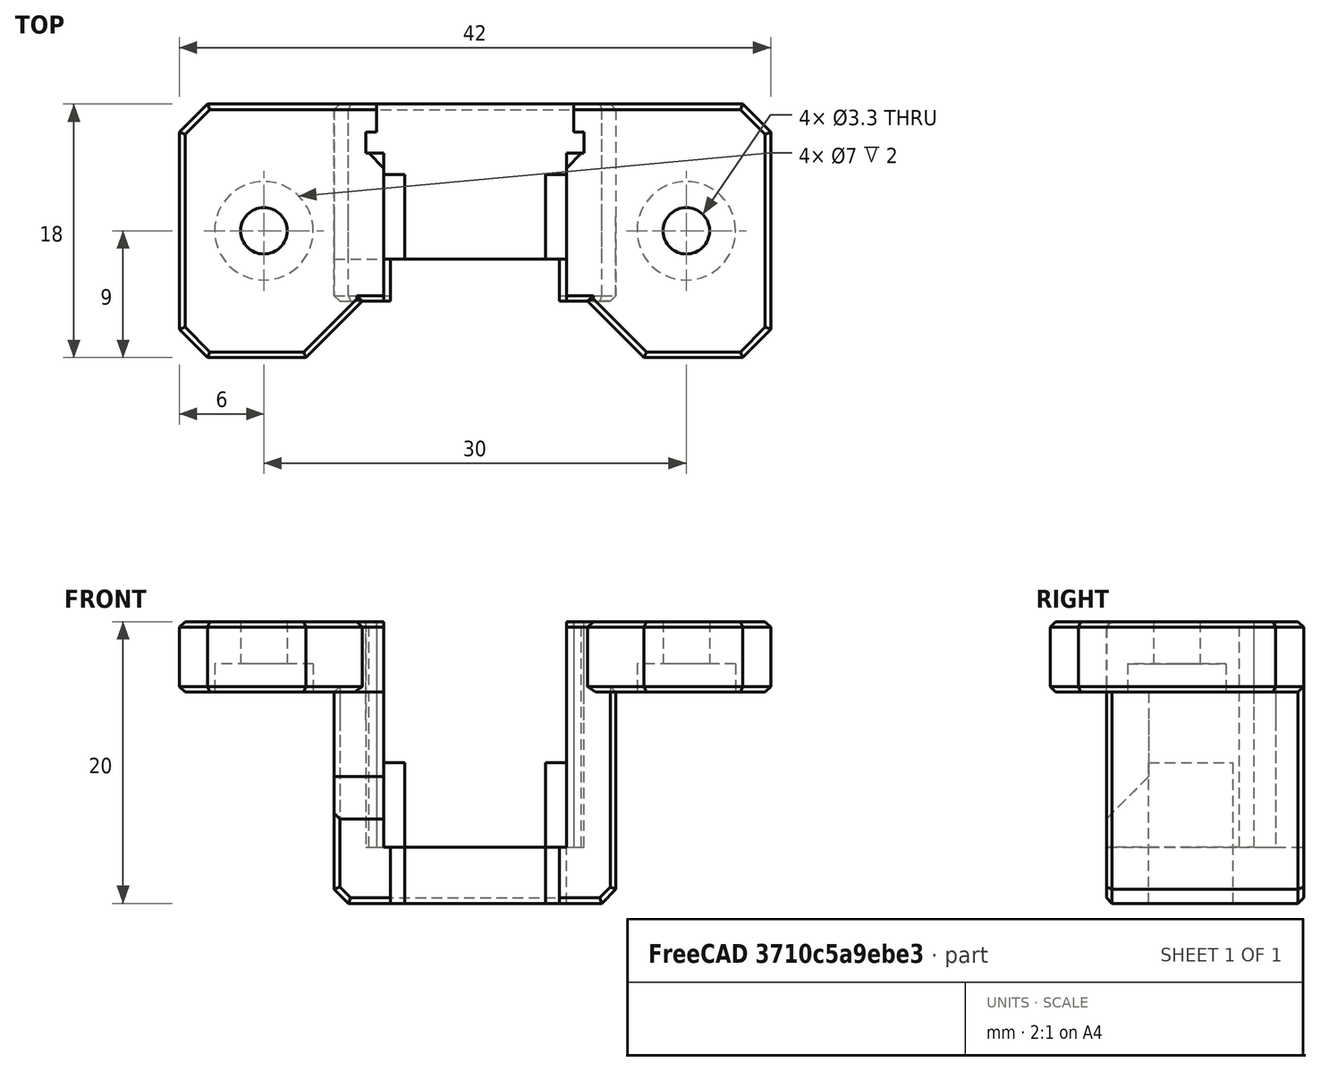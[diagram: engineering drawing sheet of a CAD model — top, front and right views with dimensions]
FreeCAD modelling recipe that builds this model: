
FCSTD DOCUMENT  (FreeCAD 0.18R16146 (Git))
Label: HTU2X-mounter
License: Other
LicenseURL: GPL3
objects: Part::Box×12, Part::MultiFuse×9, Part::Chamfer×7, Part::Cut×6, Part::Feature×6, Part::Cylinder×3, Part::MultiCommon×2
note: 45 computed .brp shape members not serialized (recipe doc carries the construction recipe); baked Part::Feature solids carry a one-line shape summary decoded from their .brp

FEATURE [Part::Box] Box  label="Cube"
  AttacherType = Attacher::AttachEngine3D
  Height = 9
  Length = 13
  Placement = pos=(-6.5,0,-2) rot=(0,0,1;0rad)
  Width = 15
FEATURE [Part::Box] Box001  label="Cube001"
  AttacherType = Attacher::AttachEngine3D
  Height = 2
  Length = 15.5
  Placement = pos=(-7.75,0,7) rot=(0,0,1;0rad)
  Width = 15
FEATURE [Part::MultiFuse] Fusion
  Shapes = -> [Box001,Box]
FEATURE [Part::Box] Box002  label="Cube002"
  AttacherType = Attacher::AttachEngine3D
  Height = 11
  Length = 20
  Placement = pos=(-10,0,0) rot=(0,0,1;0rad)
  Width = 19
FEATURE [Part::Cut] Cut
  Base = -> Box002
  Tool = -> Fusion
FEATURE [Part::Box] Box003  label="Cube003"
  AttacherType = Attacher::AttachEngine3D
  Height = 10
  Length = 14
  Placement = pos=(-7,0,8) rot=(0,0,1;0rad)
  Width = 15
FEATURE [Part::Cut] Cut001
  Base = -> Cut
  Placement = pos=(0,4e-15,19) rot=(-1,0,0;1.5708rad)
  Tool = -> Box003
FEATURE [Part::Cylinder] Cylinder
  Angle = 360
  AttacherType = Attacher::AttachEngine3D
  Height = 10
  Placement = pos=(0,4,15) rot=(0,0,1;0rad)
  Radius = 14
FEATURE [Part::Feature] Cylinder001
  Placement = pos=(0,4,12) rot=(0,0,1;0rad)
  shape: bbox 28 x 28 x 10 mm, 3 faces (baked)
FEATURE [Part::Feature] Cut001001  label="Cut002"
  Placement = pos=(0,4e-15,19) rot=(-1,0,0;1.5708rad)
  shape: bbox 20 x 11 x 19 mm, 21 faces (baked)
FEATURE [Part::MultiCommon] Common
  Placement = pos=(0,0,1) rot=(0,0,1;0rad)
  Shapes = -> [Cylinder001,Cut001001]
FEATURE [Part::Cut] Cut001002
  Base = -> Cut001
  Tool = -> Cylinder
FEATURE [Part::MultiFuse] Fusion001
  Shapes = -> [Cut001002,Common]
FEATURE [Part::Feature] Box004001  label="Cube005"
  Placement = pos=(-11,-4,0) rot=(0,0,1;0rad)
  shape: bbox 22 x 10 x 25 mm, 6 faces (baked)
FEATURE [Part::Feature] Fusion001001  label="Fusion002"
  shape: bbox 20 x 11 x 20 mm, 53 faces (baked)
FEATURE [Part::MultiCommon] Common001
  Placement = pos=(0,-3,0) rot=(0,0,1;0rad)
  Shapes = -> [Fusion001001,Box004001]
FEATURE [Part::MultiFuse] Fusion001002
  Shapes = -> [Fusion001,Common001]
FEATURE [Part::Box] Box004002  label="Cube006"
  AttacherType = Attacher::AttachEngine3D
  Height = 10
  Length = 12
  Placement = pos=(-6,-10,0) rot=(0,0,1;0rad)
  Width = 10
FEATURE [Part::Cut] Cut001003
  Base = -> Fusion001002
  Tool = -> Box004002
FEATURE [Part::Cylinder] Cylinder002
  Angle = 360
  AttacherType = Attacher::AttachEngine3D
  Height = 10
  Placement = pos=(0,0,0) rot=(-1,0,0;1.5708rad)
  Radius = 1.65
FEATURE [Part::Cylinder] Cylinder003
  Angle = 360
  AttacherType = Attacher::AttachEngine3D
  Height = 2
  Placement = pos=(0,8,1.8e-15) rot=(-1,0,0;1.5708rad)
  Radius = 3.5
FEATURE [Part::MultiFuse] Fusion001003
  Placement = pos=(-15,0,10) rot=(0,0,1;0rad)
  Shapes = -> [Cylinder003,Cylinder002]
FEATURE [Part::Feature] Fusion001003001  label="Fusion001004"
  Placement = pos=(15,0,10) rot=(0,0,1;0rad)
  shape: bbox 7 x 10 x 7 mm, 6 faces (baked)
FEATURE [Part::Box] Box004003  label="Cube007"
  AttacherType = Attacher::AttachEngine3D
  Height = 5
  Length = 13
  Placement = pos=(8,-7,15) rot=(0,0,1;0rad)
  Width = 18
FEATURE [Part::Box] Box004004  label="Cube008"
  AttacherType = Attacher::AttachEngine3D
  Height = 5
  Length = 13
  Placement = pos=(-21,-7,15) rot=(0,0,1;0rad)
  Width = 18
FEATURE [Part::MultiFuse] Fusion001003002
  Placement = pos=(0,-8,25) rot=(-1,0,0;1.5708rad)
  Shapes = -> [Fusion001003001,Fusion001003]
FEATURE [Part::Chamfer] Chamfer002
  Base = -> Cut001003
  Edges = 4 edges r=1: [Edge9,Edge16,Edge28,Edge125]
FEATURE [Part::Chamfer] Chamfer003
  Base = -> Chamfer002
  Edges = 27 edges r=0.4: [Edge1,Edge5,Edge7,Edge9,Edge11,Edge16,Edge39,Edge44,Edge47,Edge52,Edge53,Edge76,Edge77,Edge79,Edge80,Edge82,Edge89,Edge105,Edge116,Edge122,Edge139,Edge173,Edge191,Edge192,Edge212,Edge216,Edge220]
FEATURE [Part::Box] Box004005  label="Cube009"
  AttacherType = Attacher::AttachEngine3D
  Height = 10
  Length = 1.5
  Placement = pos=(-6.5,1,0) rot=(0,0,1;0rad)
  Width = 6
FEATURE [Part::Box] Box004006  label="Cube010"
  AttacherType = Attacher::AttachEngine3D
  Height = 10
  Length = 1.5
  Placement = pos=(5,1,0) rot=(0,0,1;0rad)
  Width = 6
FEATURE [Part::MultiFuse] Fusion001003005
  Shapes = -> [Box004006,Box004005]
FEATURE [Part::MultiFuse] Fusion001003006
  Shapes = -> [Box004004,Box004003]
FEATURE [Part::Chamfer] Chamfer
  Base = -> Fusion001003006
  Edges = 4 edges r=2: [Edge1,Edge3,Edge17,Edge19]
FEATURE [Part::Chamfer] Chamfer004
  Base = -> Chamfer
  Edges = 2 edges r=4: [Edge17,Edge36]
FEATURE [Part::Chamfer] Chamfer005
  Base = -> Chamfer004
  Edges = 28 edges r=0.4: [Edge1,Edge2,Edge3,Edge4,Edge5,Edge6,Edge7,Edge8,Edge11,Edge13,Edge16,Edge18,Edge19,Edge21,Edge22,Edge23,Edge24,Edge25,Edge26,Edge27,Edge28,Edge31,Edge32,Edge34,Edge36,Edge38,Edge40,Edge42]
FEATURE [Part::Cut] Cut001004
  Base = -> Chamfer005
  Tool = -> Fusion001003002
FEATURE [Part::MultiFuse] Fusion001003007
  Shapes = -> [Cut001004,Chamfer003]
FEATURE [Part::Box] Box004007  label="Cube011"
  AttacherType = Attacher::AttachEngine3D
  Height = 9
  Length = 10
  Placement = pos=(-10,-10,6) rot=(0,0,1;0rad)
  Width = 10
FEATURE [Part::Chamfer] Chamfer006
  Base = -> Box004007
  Edges = 1 edges r=3: [Edge11]
FEATURE [Part::Cut] Cut001005
  Base = -> Fusion001003007
  Placement = pos=(0,1,0) rot=(0,0,1;0rad)
  Tool = -> Chamfer006
FEATURE [Part::Box] Box004008  label="Cube012"
  AttacherType = Attacher::AttachEngine3D
  Height = 20
  Length = 2
  Placement = pos=(6.5,6.5,0) rot=(0,0,1;0rad)
  Width = 2
FEATURE [Part::Box] Box004009  label="Cube013"
  AttacherType = Attacher::AttachEngine3D
  Height = 20
  Length = 2
  Placement = pos=(-8.5,6.5,0) rot=(0,0,1;0rad)
  Width = 2
FEATURE [Part::MultiFuse] Fusion001003008
  Shapes = -> [Cut001005,Box004008,Box004009]
FEATURE [Part::Feature] Fusion001003008001  label="Fusion001003009"
  shape: bbox 42 x 18 x 20 mm, 84 faces (baked)
FEATURE [Part::Chamfer] Chamfer007
  Base = -> Fusion001003008001
  Edges = 2 edges r=1.05: [Edge75,Edge94]
